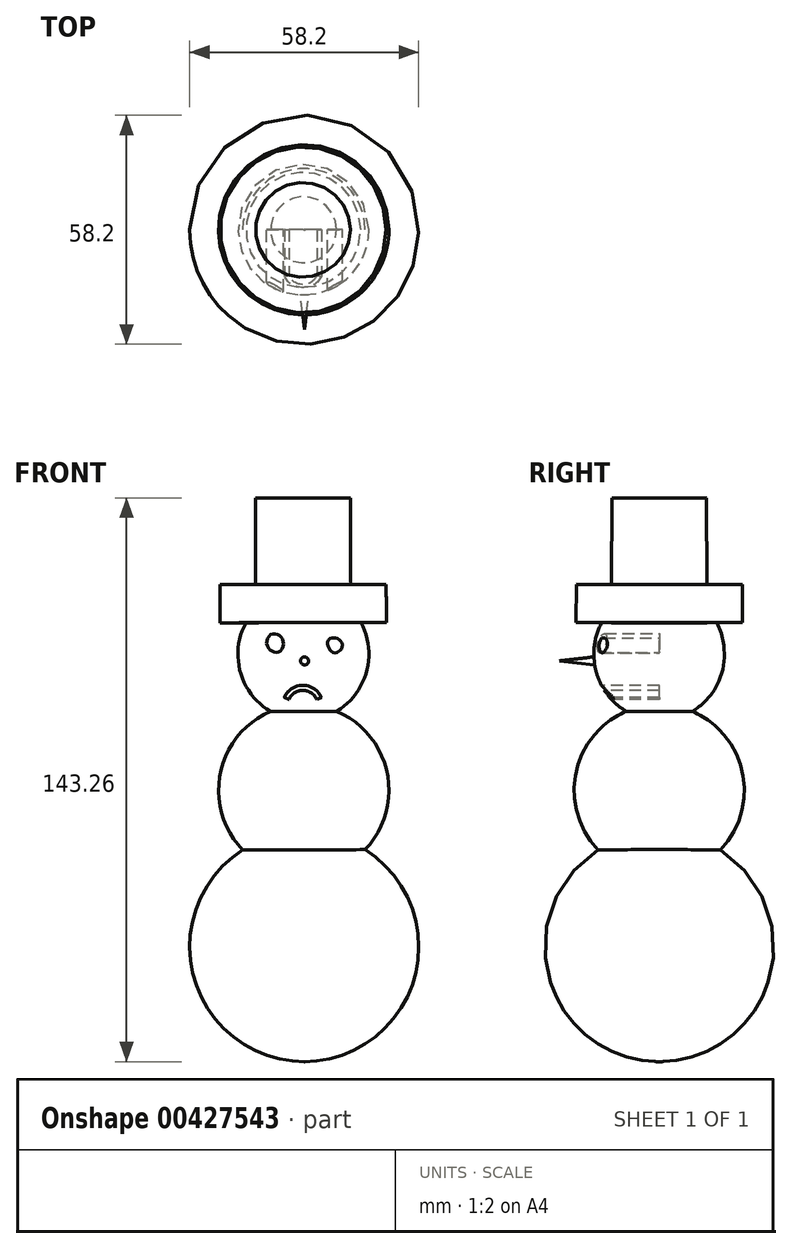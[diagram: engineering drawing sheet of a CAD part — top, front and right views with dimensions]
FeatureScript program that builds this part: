
annotation { "Feature Type Name" : "Feature", "Feature Type Description" : "" }
export const myFeature = defineFeature(function(context is Context, id is Id, definition is map)
    precondition{}
    {
        {
            var Q0;
            Q0=qCreatedBy(makeId("Front.planeOp"),FACE);
            var sketch = newSketch(context, id + "F0", { "sketchPlane" : qUnion([Q0])});
            skArc(sketch, "E0", {"start": v(-15.7, 24.6) * mm, "mid": v(0, -29.18) * mm, "end": v(15.7, 24.6) * mm});
            skArc(sketch, "E1", {"start": v(-8.65, 59.8) * mm, "mid": v(-21.4, 44.05) * mm, "end": v(-15.7, 24.6) * mm});
            skArc(sketch, "E2", {"start": v(8.65, 59.8) * mm, "mid": v(16.3, 69.81) * mm, "end": v(14.92, 82.33) * mm});
            skPoint(sketch, "E3.orphan", {"position": v(0, 91.27) * mm});
            skArc(sketch, "E4.trimOffspring", {"start": v(15.7, 24.6) * mm, "mid": v(21.4, 44.05) * mm, "end": v(8.65, 59.8) * mm});
            skLineSegment(sketch, "E5.bottom", {"start": v(-21.42, 92) * mm, "end": v(-12.42, 92) * mm});
            skLineSegment(sketch, "E5.top", {"start": v(-21.42, 82.33) * mm, "end": v(-14.92, 82.33) * mm});
            skLineSegment(sketch, "E5.left", {"start": v(-21.42, 92) * mm, "end": v(-21.42, 82.33) * mm});
            skLineSegment(sketch, "E5.right", {"start": v(22.1, 92) * mm, "end": v(22.1, 82.33) * mm});
            skLineSegment(sketch, "E6.top", {"start": v(-12.42, 114.01) * mm, "end": v(11.63, 114.01) * mm});
            skLineSegment(sketch, "E6.left", {"start": v(-12.42, 92) * mm, "end": v(-12.42, 114.01) * mm});
            skLineSegment(sketch, "E6.right", {"start": v(11.63, 92) * mm, "end": v(11.63, 114.01) * mm});
            skArc(sketch, "E7.trimOffspring", {"start": v(-14.92, 82.33) * mm, "mid": v(-16.3, 69.81) * mm, "end": v(-8.65, 59.8) * mm});
            skLineSegment(sketch, "E8.trimOffspring", {"start": v(11.63, 92) * mm, "end": v(22.1, 92) * mm});
            skLineSegment(sketch, "E9.trimOffspring", {"start": v(14.92, 82.33) * mm, "end": v(22.1, 82.33) * mm});
            skPoint(sketch, "E10.end.orphan", {"position": v(0, -29.18) * mm});
            skLineSegment(sketch, "E11", {"start": v(-0.4, 114.01) * mm, "end": v(0, -29.18) * mm});
            skSolve(sketch);
        }
        {
            var Q0;
            {var subQ0=sQuery(id+"F0.wireOp",EDGE,"E1");Q0=makeQuery(id+"F0.imprint","IMPRINT",FACE,{"disambiguationData":[TD([[makeQuery(id+"F0.imprint","IMPRINT",EDGE,{"derivedFrom":subQ0}),1.0]])]});}
            var Q1;
            Q1=sQuery(id+"F0.wireOp",EDGE,"E11");
            revolve(context, id + "F1", {"entities" : qUnion([Q0]), "axis" : qUnion([Q1]), "revolveType" : RevolveType.FULL});
        }
        {
            var Q0;
            Q0=qCreatedBy(makeId("Front.planeOp"),FACE);
            cPlane(context, id + "F2", {"entities" : qUnion([Q0]), "cplaneType" : CPlaneType.OFFSET, "offset" : 25.4 * mm, "width" : 152.4 * mm, "height" : 152.4 * mm});
        }
        {
            var Q0;
            Q0=qCreatedBy(id+"F2.planeOp",FACE);
            var sketch = newSketch(context, id + "F3", { "sketchPlane" : qUnion([Q0])});
            skPoint(sketch, "E12", {"position": v(0, 72.66) * mm});
            skFitSpline(sketch, "E13", {"points": [v(-8.03, 79.53) * mm, v(-9.47, 78.09) * mm, v(-9, 75.67) * mm, v(-6.34, 74.95) * mm, v(-5.37, 77.36) * mm, v(-6.1, 78.81) * mm, v(-8.03, 79.53) * mm]});
            skFitSpline(sketch, "E14", {"points": [v(8.38, 78.33) * mm, v(6.2, 78.09) * mm, v(5.97, 76.4) * mm, v(7.66, 74.7) * mm, v(9.59, 76.16) * mm, v(8.38, 78.33) * mm]});
            skArc(sketch, "E15", {"start": v(4.28, 63.37) * mm, "mid": v(-0.43, 66.43) * mm, "end": v(-5.13, 63.37) * mm});
            skArc(sketch, "E16.0", {"start": v(3.12, 62.85) * mm, "mid": v(-0.43, 65.16) * mm, "end": v(-3.97, 62.85) * mm});
            skLineSegment(sketch, "E17", {"start": v(-5.13, 63.37) * mm, "end": v(-3.97, 62.85) * mm});
            skLineSegment(sketch, "E18", {"start": v(3.12, 62.85) * mm, "end": v(4.28, 63.37) * mm});
            skSolve(sketch);
        }
        {
            var Q0;
            Q0=qCreatedBy(makeId("Front.planeOp"),FACE);
            var sketch = newSketch(context, id + "F4", { "sketchPlane" : qUnion([Q0])});
            skCircle(sketch, "E19", {"center": v(0, 72.66) * mm, "radius": 2.93 * mm});
            skSolve(sketch);
        }
        {
            var Q1;
            Q1=sQuery(id+"F3.wireOp",VERTEX,"E12");
            var Q2;
            Q2 = qSketchRegion(id + "F4", true);
            loft(context, id + "F5", {"operationType" : NewBodyOperationType.ADD, "sheetProfilesArray" : [{ "sheetProfileEntities" : qUnion([Q1]) }, { "sheetProfileEntities" : qUnion([Q2]) }]});
        }
        {
            var Q0;
            Q0 = qSketchRegion(id + "F3", true);
            extrude(context, id + "F6", {"entities" : qUnion([Q0]), "operationType" : NewBodyOperationType.REMOVE, "oppositeDirection" : true, "depth" : 25.4 * mm});
        }
    });
